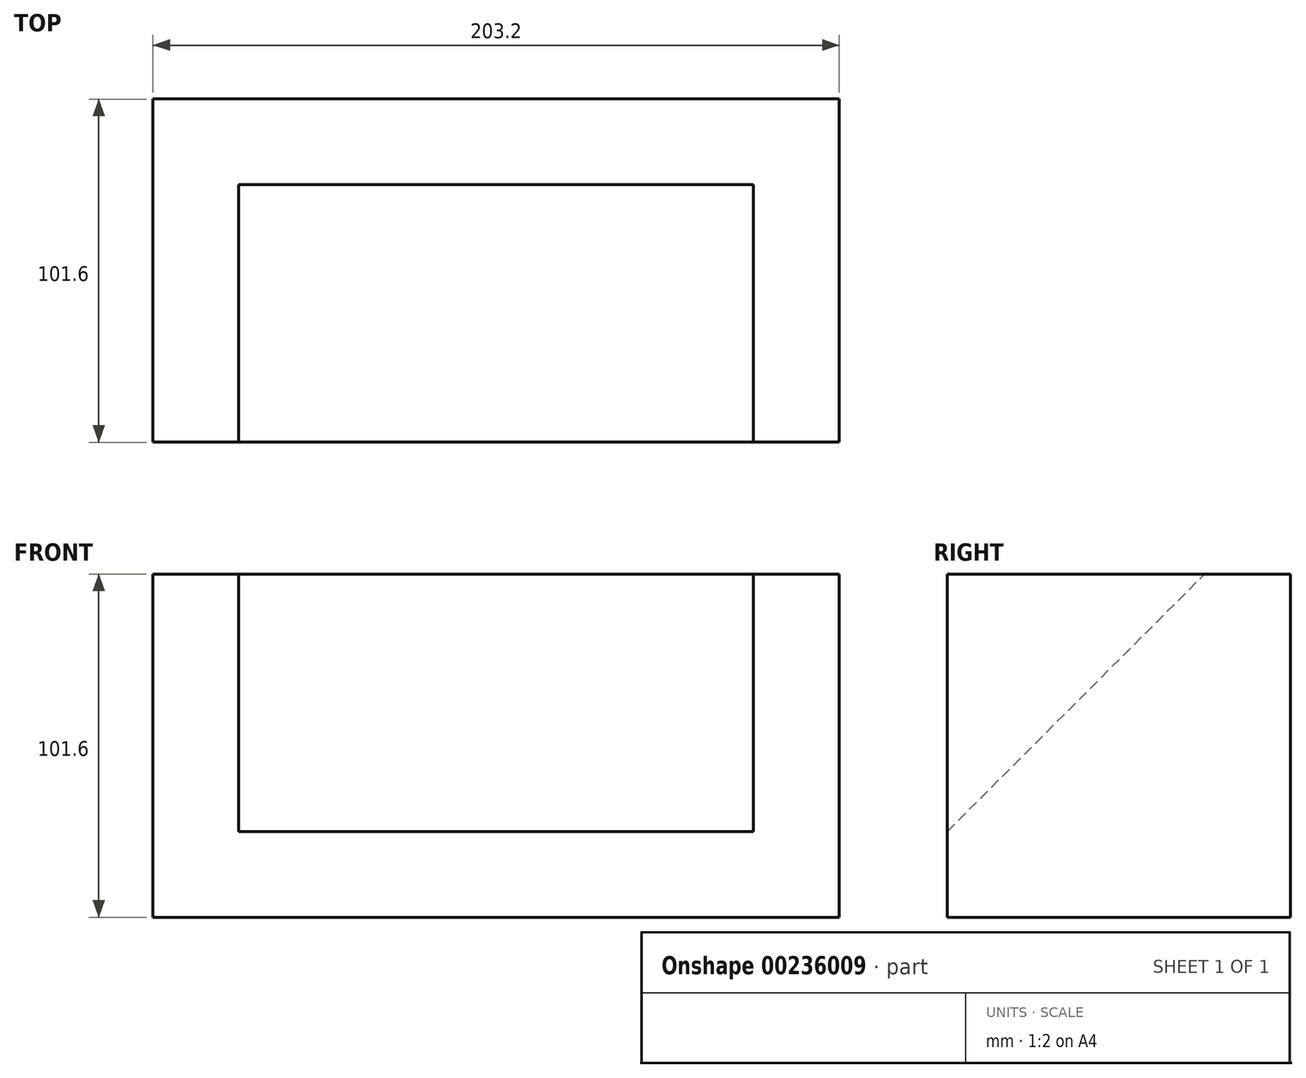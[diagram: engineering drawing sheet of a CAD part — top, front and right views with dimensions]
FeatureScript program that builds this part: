
annotation { "Feature Type Name" : "Feature", "Feature Type Description" : "" }
export const myFeature = defineFeature(function(context is Context, id is Id, definition is map)
    precondition{}
    {
        {
            var Q0;
            Q0=qCreatedBy(makeId("Top.planeOp"),FACE);
            var sketch = newSketch(context, id + "F0", { "sketchPlane" : qUnion([Q0])});
            skLineSegment(sketch, "E0.bottom", {"start": v(-83.12, -16.87) * mm, "end": v(120.08, -16.87) * mm});
            skLineSegment(sketch, "E0.top", {"start": v(-83.12, 84.73) * mm, "end": v(120.08, 84.73) * mm});
            skLineSegment(sketch, "E0.left", {"start": v(-83.12, -16.87) * mm, "end": v(-83.12, 84.73) * mm});
            skLineSegment(sketch, "E0.right", {"start": v(120.08, -16.87) * mm, "end": v(120.08, 84.73) * mm});
            skSolve(sketch);
        }
        {
            var Q0;
            Q0=makeQuery(id+"F0.imprint","IMPRINT",FACE,{"disambiguationData":[TD([[makeQuery(id+"F0.imprint","IMPRINT",EDGE,{"derivedFrom":sQuery(id+"F0.wireOp",EDGE,"E0.bottom")}),1.0]])]});
            extrude(context, id + "F1", {"entities" : qUnion([Q0]), "depth" : 101.6 * mm});
        }
        {
            var Q0;
            Q0=makeQuery(id+"F1.opExtrude","CAP_FACE",FACE,{"disambiguationData":[OSD([sQuery(id+"F0.wireOp",EDGE,"E0.bottom"),sQuery(id+"F0.wireOp",EDGE,"E0.top"),sQuery(id+"F0.wireOp",EDGE,"E0.left"),sQuery(id+"F0.wireOp",EDGE,"E0.right")])],"isStart":false});
            var sketch = newSketch(context, id + "F2", { "sketchPlane" : qUnion([Q0])});
            skLineSegment(sketch, "E1", {"start": v(-83.12, -16.87) * mm, "end": v(-57.72, -16.87) * mm});
            skLineSegment(sketch, "E2", {"start": v(120.08, -16.87) * mm, "end": v(94.68, -16.87) * mm});
            skLineSegment(sketch, "E3", {"start": v(94.68, -16.87) * mm, "end": v(94.68, 59.33) * mm});
            skLineSegment(sketch, "E4", {"start": v(-57.72, -16.87) * mm, "end": v(-57.72, 59.33) * mm});
            skLineSegment(sketch, "E5", {"start": v(-57.72, 59.33) * mm, "end": v(94.68, 59.33) * mm});
            skSolve(sketch);
        }
        {
            var Q0;
            {var subQ0=sQuery(id+"F2.wireOp",EDGE,"E3");Q0=makeQuery(id+"F2.imprint","IMPRINT",FACE,{"disambiguationData":[TD([[makeQuery(id+"F2.imprint","IMPRINT",EDGE,{"derivedFrom":subQ0}),1.0]])]});}
            extrude(context, id + "F3", {"entities" : qUnion([Q0]), "operationType" : NewBodyOperationType.REMOVE, "oppositeDirection" : true, "depth" : 76.2 * mm});
        }
        {
            var Q0;
            Q0=makeQuery(id+"F3.boolean.opBoolean","COPY",FACE,{"derivedFrom":makeQuery(id+"F3.opExtrude","SWEPT_FACE",FACE,{"disambiguationData":[OSD([sQuery(id+"F2.wireOp",EDGE,"E4")])]})});
            var sketch = newSketch(context, id + "F4", { "sketchPlane" : qUnion([Q0])});
            skLineSegment(sketch, "E6", {"start": v(-16.87, 25.4) * mm, "end": v(59.33, 101.6) * mm});
            skSolve(sketch);
        }
        {
            var Q0;
            Q0=makeQuery(id+"F4.imprint","IMPRINT",FACE,{"disambiguationData":[TD([[makeQuery(id+"F4.imprint","IMPRINT",EDGE,{"derivedFrom":sQuery(id+"F4.wireOp",EDGE,"E6")}),-1.0]])]});
            extrude(context, id + "F5", {"entities" : qUnion([Q0]), "operationType" : NewBodyOperationType.ADD, "depth" : 127 * mm});
        }
        {
            var Q0;
            Q0=makeQuery(id+"F5.opExtrude","CAP_FACE",FACE,{"disambiguationData":[OSD([sQuery(id+"F2.wireOp",EDGE,"E4"),sQuery(id+"F2.wireOp",EDGE,"E5"),sQuery(id+"F4.wireOp",EDGE,"E6")])],"isStart":false});
            extrude(context, id + "F6", {"entities" : qUnion([Q0]), "operationType" : NewBodyOperationType.ADD, "depth" : 25.4 * mm});
        }
    });
